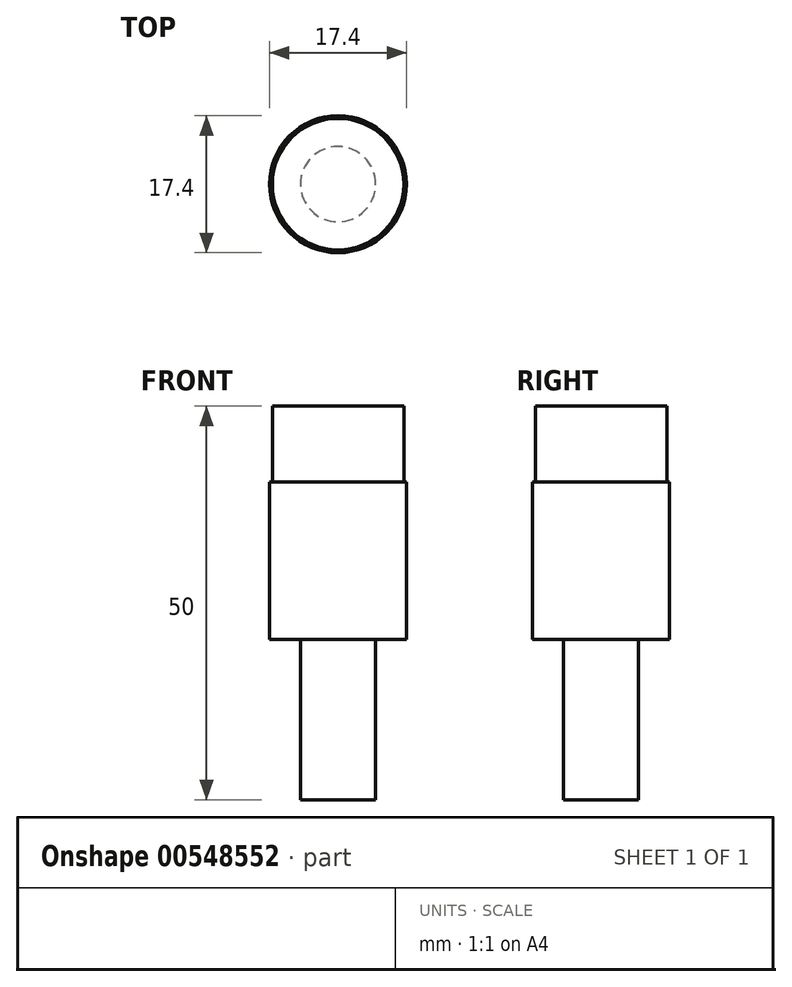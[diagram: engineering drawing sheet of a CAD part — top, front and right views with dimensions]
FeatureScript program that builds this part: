
annotation { "Feature Type Name" : "Feature", "Feature Type Description" : "" }
export const myFeature = defineFeature(function(context is Context, id is Id, definition is map)
    precondition{}
    {
        {
            var Q0;
            Q0=qCreatedBy(makeId("Top.planeOp"),FACE);
            var sketch = newSketch(context, id + "F0", { "sketchPlane" : qUnion([Q0])});
            skCircle(sketch, "E0", {"center": v(0, 0) * mm, "radius": 8.7 * mm});
            skSolve(sketch);
        }
        {
            var Q0;
            Q0=qSketchRegion(id+"F0",true);
            extrude(context, id + "F1", {"entities" : qUnion([Q0]), "depth" : 20 * mm, "offsetDistance" : 25.4 * mm});
        }
        {
            var Q0;
            Q0=makeQuery(id+"F1.opExtrude","CAP_FACE",FACE,{"disambiguationData":[OSD([sQuery(id+"F0.wireOp",EDGE,"E0")])],"isStart":false});
            var sketch = newSketch(context, id + "F2", { "sketchPlane" : qUnion([Q0])});
            skCircle(sketch, "E1", {"center": v(0, 0) * mm, "radius": 8.35 * mm});
            skSolve(sketch);
        }
        {
            var Q0;
            Q0=qSketchRegion(id+"F2",true);
            extrude(context, id + "F3", {"entities" : qUnion([Q0]), "operationType" : NewBodyOperationType.ADD, "depth" : 9.6 * mm, "offsetDistance" : 25.4 * mm});
        }
        {
            var Q0;
            Q0=makeQuery(id+"F1.opExtrude","CAP_FACE",FACE,{"disambiguationData":[OSD([sQuery(id+"F0.wireOp",EDGE,"E0")])],"isStart":true});
            var sketch = newSketch(context, id + "F4", { "sketchPlane" : qUnion([Q0])});
            skCircle(sketch, "E2", {"center": v(0, 0) * mm, "radius": 4.78 * mm});
            skSolve(sketch);
        }
        {
            var Q0;
            Q0 = qSketchRegion(id + "F4", true);
            extrude(context, id + "F5", {"entities" : qUnion([Q0]), "operationType" : NewBodyOperationType.ADD, "depth" : 20.4 * mm, "offsetDistance" : 25 * mm});
        }
    });
